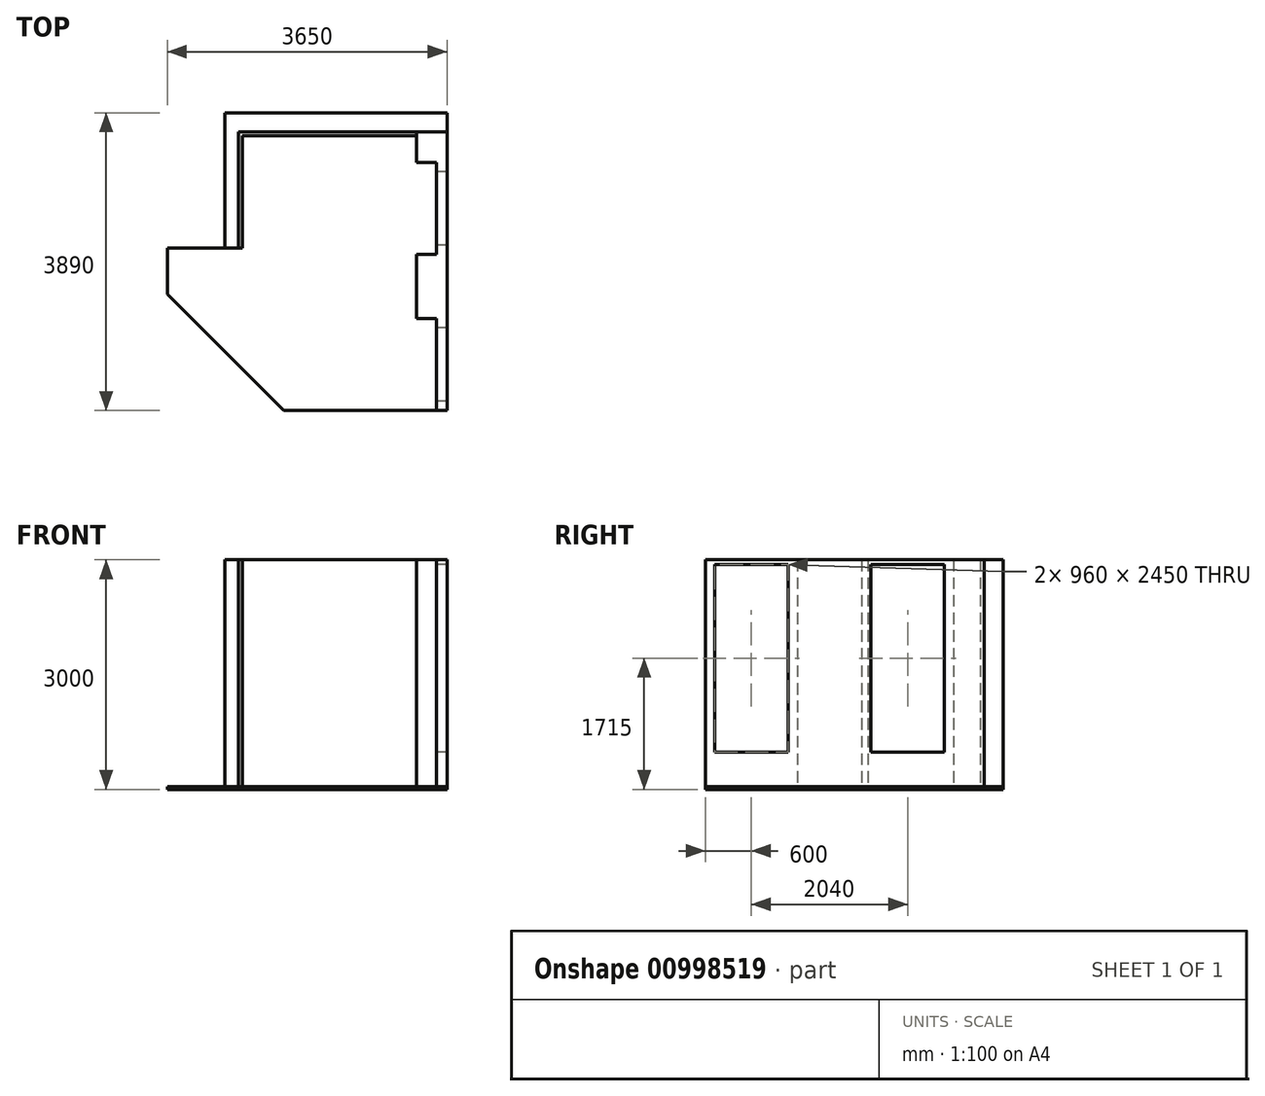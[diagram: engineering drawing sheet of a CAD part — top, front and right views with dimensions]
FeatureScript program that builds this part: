
annotation { "Feature Type Name" : "Feature", "Feature Type Description" : "" }
export const myFeature = defineFeature(function(context is Context, id is Id, definition is map)
    precondition{}
    {
        {
            var Q0;
            Q0=qCreatedBy(makeId("Top.planeOp"),FACE);
            var sketch = newSketch(context, id + "F0", { "sketchPlane" : qUnion([Q0])});
            skLineSegment(sketch, "E0", {"start": v(0, 0) * mm, "end": v(-50, 0) * mm});
            skLineSegment(sketch, "E1", {"start": v(-50, 0) * mm, "end": v(-50, 1520) * mm});
            skLineSegment(sketch, "E2", {"start": v(0, 0) * mm, "end": v(0, 1470) * mm});
            skLineSegment(sketch, "E3", {"start": v(0, 1470) * mm, "end": v(2270, 1470) * mm});
            skLineSegment(sketch, "E4", {"start": v(2270, 1470) * mm, "end": v(2270, 1120) * mm});
            skLineSegment(sketch, "E5", {"start": v(2270, 1120) * mm, "end": v(2530, 1120) * mm});
            skLineSegment(sketch, "E6", {"start": v(2530, 1120) * mm, "end": v(2530, -80) * mm});
            skLineSegment(sketch, "E7", {"start": v(2530, -80) * mm, "end": v(2270, -80) * mm});
            skLineSegment(sketch, "E8", {"start": v(-50, 1520) * mm, "end": v(2670, 1520) * mm});
            skLineSegment(sketch, "E9", {"start": v(2670, 1520) * mm, "end": v(2670, -2120) * mm});
            skLineSegment(sketch, "E10", {"start": v(2670, -2120) * mm, "end": v(2530, -2120) * mm});
            skLineSegment(sketch, "E11", {"start": v(2530, -920) * mm, "end": v(2530, -2120) * mm});
            skLineSegment(sketch, "E12", {"start": v(2530, -920) * mm, "end": v(2270, -920) * mm});
            skLineSegment(sketch, "E13", {"start": v(2270, -920) * mm, "end": v(2270, -80) * mm});
            skLineSegment(sketch, "E14", {"start": v(2270, 1470) * mm, "end": v(2270, 1520) * mm});
            skLineSegment(sketch, "E15", {"start": v(-50, 0) * mm, "end": v(-230, 0) * mm});
            skLineSegment(sketch, "E16", {"start": v(-230, 0) * mm, "end": v(-230, 1770) * mm});
            skLineSegment(sketch, "E17", {"start": v(-230, 1770) * mm, "end": v(2670, 1770) * mm});
            skLineSegment(sketch, "E18", {"start": v(2670, 1770) * mm, "end": v(2670, 1520) * mm});
            skSolve(sketch);
        }
        {
            var Q0;
            Q0=makeQuery(id+"F0.imprint","IMPRINT",FACE,{"disambiguationData":[TD([[makeQuery(id+"F0.imprint","IMPRINT",EDGE,{"derivedFrom":sQuery(id+"F0.wireOp",EDGE,"E0")}),-1.0]])]});
            extrude(context, id + "F1", {"entities" : qUnion([Q0]), "depth" : 2960 * mm, "offsetDistance" : 25 * mm});
        }
        {
            var Q0;
            Q0=makeQuery(id+"F0.imprint","IMPRINT",FACE,{"disambiguationData":[TD([[makeQuery(id+"F0.imprint","IMPRINT",EDGE,{"derivedFrom":sQuery(id+"F0.wireOp",EDGE,"E4")}),1.0]])]});
            var Q1;
            Q1=makeQuery(id+"F1.opExtrude","CAP_FACE",FACE,{"disambiguationData":[OSD([sQuery(id+"F0.wireOp",EDGE,"E0"),sQuery(id+"F0.wireOp",EDGE,"E1"),sQuery(id+"F0.wireOp",EDGE,"E2"),sQuery(id+"F0.wireOp",EDGE,"E3"),sQuery(id+"F0.wireOp",EDGE,"E8"),sQuery(id+"F0.wireOp",EDGE,"E14")])],"isStart":false});
            extrude(context, id + "F2", {"entities" : qUnion([Q0]), "endBound" : BoundingType.UP_TO_SURFACE, "depth" : 25 * mm, "endBoundEntityFace" : qUnion([Q1]), "offsetDistance" : 25 * mm});
        }
        {
            var Q0;
            {var subQ3=sQuery(id+"F0.wireOp",EDGE,"E1");Q0=makeQuery(id+"F0.imprint","IMPRINT",FACE,{"disambiguationData":[TD([[makeQuery(id+"F0.imprint","IMPRINT",EDGE,{"derivedFrom":subQ3}),1.0]])]});}
            var Q1;
            Q1=makeQuery(id+"F1.opExtrude","CAP_FACE",FACE,{"disambiguationData":[OSD([sQuery(id+"F0.wireOp",EDGE,"E0"),sQuery(id+"F0.wireOp",EDGE,"E1"),sQuery(id+"F0.wireOp",EDGE,"E2"),sQuery(id+"F0.wireOp",EDGE,"E3"),sQuery(id+"F0.wireOp",EDGE,"E8"),sQuery(id+"F0.wireOp",EDGE,"E14")])],"isStart":false});
            extrude(context, id + "F3", {"entities" : qUnion([Q0]), "endBound" : BoundingType.UP_TO_SURFACE, "depth" : 25 * mm, "endBoundEntityFace" : qUnion([Q1]), "offsetDistance" : 25 * mm});
        }
        {
            var Q0;
            Q0=makeQuery(id+"F2.opExtrude","SWEPT_FACE",FACE,{"disambiguationData":[OSD([sQuery(id+"F0.wireOp",EDGE,"E6")])]});
            var sketch = newSketch(context, id + "F4", { "sketchPlane" : qUnion([Q0])});
            skLineSegment(sketch, "E19.bottom", {"start": v(-1000, 2900) * mm, "end": v(-40, 2900) * mm});
            skLineSegment(sketch, "E19.top", {"start": v(-1000, 450) * mm, "end": v(-40, 450) * mm});
            skLineSegment(sketch, "E19.left", {"start": v(-1000, 2900) * mm, "end": v(-1000, 450) * mm});
            skLineSegment(sketch, "E19.right", {"start": v(-40, 2900) * mm, "end": v(-40, 450) * mm});
            skPoint(sketch, "E19.middle", {"position": v(-520, 1675) * mm});
            skLineSegment(sketch, "E20.bottom", {"start": v(1040, 2900) * mm, "end": v(2000, 2900) * mm});
            skLineSegment(sketch, "E20.top", {"start": v(1040, 450) * mm, "end": v(2000, 450) * mm});
            skLineSegment(sketch, "E20.left", {"start": v(1040, 2900) * mm, "end": v(1040, 450) * mm});
            skLineSegment(sketch, "E20.right", {"start": v(2000, 2900) * mm, "end": v(2000, 450) * mm});
            skPoint(sketch, "E20.middle", {"position": v(1520, 1675) * mm});
            skLineSegment(sketch, "E21", {"start": v(-1120, 1675) * mm, "end": v(80, 1675) * mm, "construction": true});
            skLineSegment(sketch, "E22", {"start": v(920, 1675) * mm, "end": v(2120, 1675) * mm, "construction": true});
            skSolve(sketch);
        }
        {
            var Q0;
            Q0 = qSketchRegion(id + "F4", true);
            extrude(context, id + "F5", {"entities" : qUnion([Q0]), "operationType" : NewBodyOperationType.REMOVE, "endBound" : BoundingType.THROUGH_ALL, "oppositeDirection" : true, "depth" : 25 * mm, "offsetDistance" : 25 * mm});
        }
        {
            var Q0;
            Q0=qCreatedBy(makeId("Top.planeOp"),FACE);
            var sketch = newSketch(context, id + "F6", { "sketchPlane" : qUnion([Q0])});
            skLineSegment(sketch, "E23.0", {"start": v(-230, 0) * mm, "end": v(-230, 1770) * mm});
            skLineSegment(sketch, "E23.1", {"start": v(-230, 1770) * mm, "end": v(2670, 1770) * mm});
            skLineSegment(sketch, "E23.2", {"start": v(2670, 1520) * mm, "end": v(2670, -2120) * mm});
            skLineSegment(sketch, "E24.0", {"start": v(2670, 1770) * mm, "end": v(2670, 1520) * mm});
            skLineSegment(sketch, "E25", {"start": v(-230, 0) * mm, "end": v(-980, 0) * mm});
            skLineSegment(sketch, "E26", {"start": v(540, -2120) * mm, "end": v(2670, -2120) * mm});
            skLineSegment(sketch, "E27", {"start": v(-980, 0) * mm, "end": v(-980, -600) * mm});
            skLineSegment(sketch, "E28", {"start": v(-980, -600) * mm, "end": v(540, -2120) * mm});
            skSolve(sketch);
        }
        {
            var Q0;
            Q0 = qSketchRegion(id + "F6", true);
            extrude(context, id + "F7", {"entities" : qUnion([Q0]), "oppositeDirection" : true, "depth" : 40 * mm, "offsetDistance" : 25 * mm});
        }
    });
